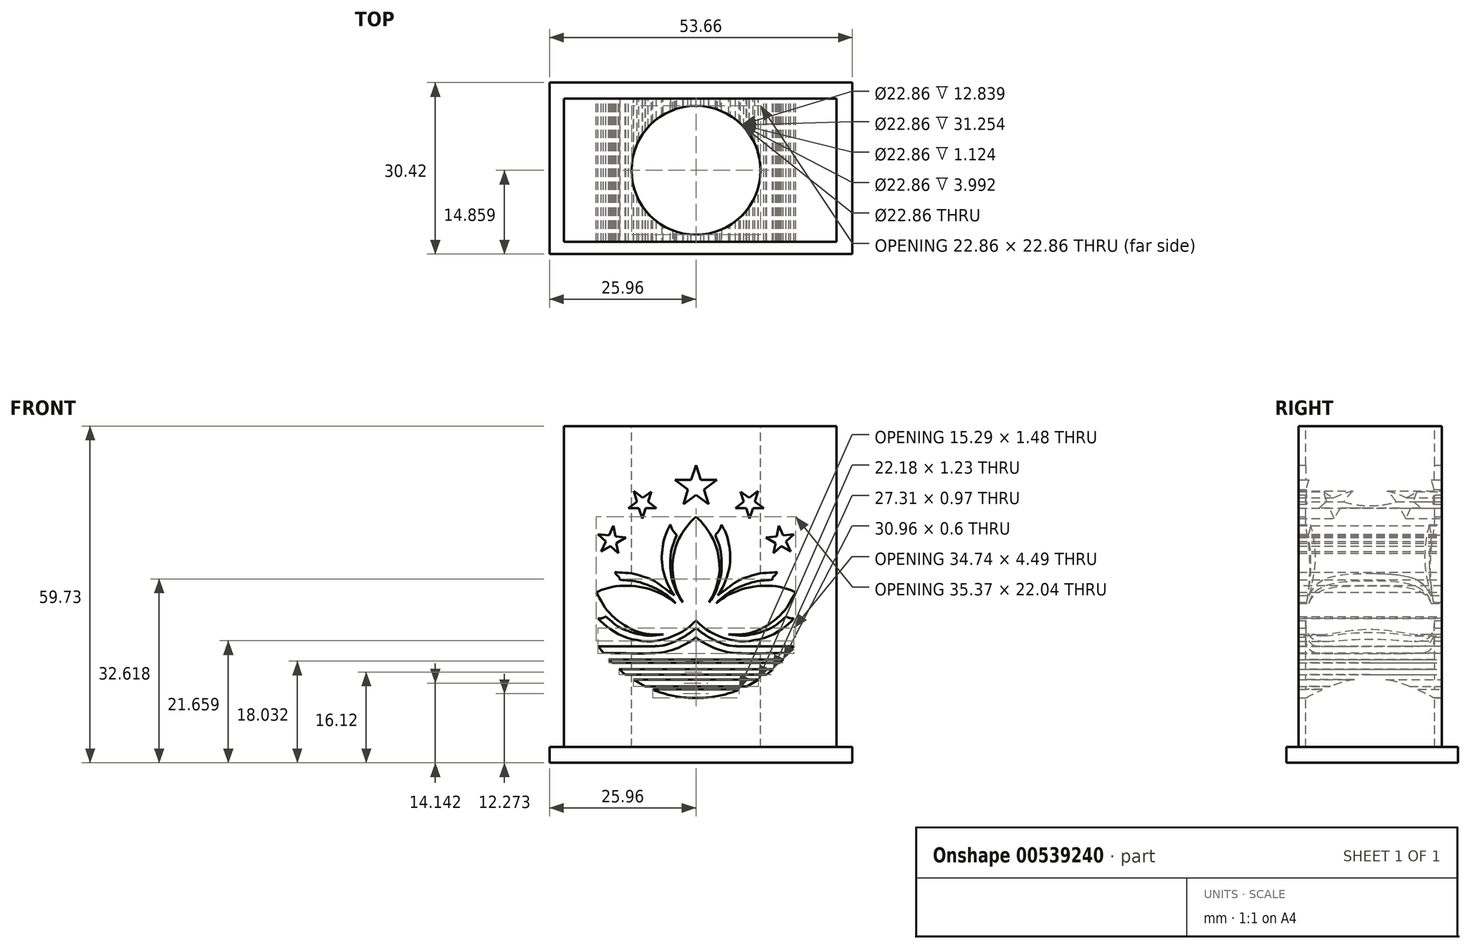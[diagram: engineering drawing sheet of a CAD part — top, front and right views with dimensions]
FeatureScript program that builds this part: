
annotation { "Feature Type Name" : "Feature", "Feature Type Description" : "" }
export const myFeature = defineFeature(function(context is Context, id is Id, definition is map)
    precondition{}
    {
        {
            var Q0;
            Q0=qCreatedBy(makeId("Front.planeOp"),FACE);
            var sketch = newSketch(context, id + "F0", { "sketchPlane" : qUnion([Q0])});
            skLineSegment(sketch, "E0.bottom", {"start": v(-23.4, 10.65) * mm, "end": v(24.88, 10.65) * mm});
            skLineSegment(sketch, "E0.top", {"start": v(-23.4, -46.28) * mm, "end": v(24.88, -46.28) * mm});
            skLineSegment(sketch, "E0.left", {"start": v(-23.4, 10.65) * mm, "end": v(-23.4, -46.28) * mm});
            skLineSegment(sketch, "E0.right", {"start": v(24.88, 10.65) * mm, "end": v(24.88, -46.28) * mm});
            skLineSegment(sketch, "E1", {"start": v(-14.67, -7.02) * mm, "end": v(-15.43, -8.75) * mm});
            skLineSegment(sketch, "E2", {"start": v(-15.43, -8.75) * mm, "end": v(-17.36, -8.56) * mm});
            skLineSegment(sketch, "E3", {"start": v(-17.36, -8.56) * mm, "end": v(-15.96, -9.83) * mm});
            skLineSegment(sketch, "E4", {"start": v(-15.96, -9.83) * mm, "end": v(-16.8, -11.56) * mm});
            skLineSegment(sketch, "E5", {"start": v(-16.8, -11.56) * mm, "end": v(-15.16, -10.63) * mm});
            skLineSegment(sketch, "E6", {"start": v(-15.16, -10.63) * mm, "end": v(-13.74, -11.88) * mm});
            skLineSegment(sketch, "E7", {"start": v(-13.74, -11.88) * mm, "end": v(-14.13, -10.12) * mm});
            skLineSegment(sketch, "E8", {"start": v(-14.13, -10.12) * mm, "end": v(-12.4, -9.14) * mm});
            skLineSegment(sketch, "E9", {"start": v(-12.4, -9.14) * mm, "end": v(-14.28, -8.92) * mm});
            skLineSegment(sketch, "E10", {"start": v(-14.67, -7.02) * mm, "end": v(-14.28, -8.92) * mm});
            skLineSegment(sketch, "E11", {"start": v(-11.02, -0.87) * mm, "end": v(-10.44, -2.79) * mm});
            skLineSegment(sketch, "E12", {"start": v(-10.44, -2.79) * mm, "end": v(-12.01, -3.9) * mm});
            skLineSegment(sketch, "E13", {"start": v(-12.01, -3.9) * mm, "end": v(-10.14, -3.9) * mm});
            skLineSegment(sketch, "E14", {"start": v(-10.14, -3.9) * mm, "end": v(-9.51, -5.75) * mm});
            skLineSegment(sketch, "E15", {"start": v(-9.51, -5.75) * mm, "end": v(-8.92, -3.9) * mm});
            skLineSegment(sketch, "E16", {"start": v(-8.92, -3.9) * mm, "end": v(-7.01, -3.9) * mm});
            skLineSegment(sketch, "E17", {"start": v(-7.01, -3.9) * mm, "end": v(-8.5, -2.75) * mm});
            skLineSegment(sketch, "E18", {"start": v(-8.5, -2.75) * mm, "end": v(-7.91, -0.98) * mm});
            skLineSegment(sketch, "E19", {"start": v(-7.91, -0.98) * mm, "end": v(-9.44, -2.07) * mm});
            skLineSegment(sketch, "E20", {"start": v(-9.44, -2.07) * mm, "end": v(-11.02, -0.87) * mm});
            skLineSegment(sketch, "E21", {"start": v(0, 3.74) * mm, "end": v(-0.86, 1.14) * mm});
            skLineSegment(sketch, "E22", {"start": v(-0.86, 1.14) * mm, "end": v(-3.73, 1.14) * mm});
            skLineSegment(sketch, "E23", {"start": v(-3.73, 1.14) * mm, "end": v(-1.44, -0.6) * mm});
            skLineSegment(sketch, "E24", {"start": v(-1.44, -0.6) * mm, "end": v(-2.21, -3.2) * mm});
            skLineSegment(sketch, "E25", {"start": v(-2.21, -3.2) * mm, "end": v(0, -1.55) * mm});
            skPoint(sketch, "E26.1.internal.snap0", {"position": v(-1.1, -2.38) * mm});
            skFitSpline(sketch, "E26", {"points": [v(0, -5.44) * mm, v(-1.1, -6.5) * mm, v(-2.36, -8.25) * mm, v(-3.29, -9.91) * mm, v(-4.02, -12.68) * mm, v(-4.12, -15.63) * mm, v(-3.2, -19) * mm, v(-2.32, -20.6) * mm], "startDerivative": vector(-9.56, -8.22) * mm, "endDerivative": vector(6.99, -11.2) * mm});
            skFitSpline(sketch, "E27", {"points": [v(-3.43, -8.7) * mm, v(-3.83, -9.72) * mm, v(-4.32, -11.27) * mm, v(-4.53, -13.34) * mm, v(-4.52, -14.72) * mm, v(-4.32, -16.29) * mm, v(-3.8, -17.9) * mm, v(-3.26, -19.24) * mm, v(-2.32, -20.6) * mm], "startDerivative": vector(-3.76, -9.37) * mm, "endDerivative": vector(8.12, -10.53) * mm});
            skFitSpline(sketch, "E28", {"points": [v(-4.54, -6.83) * mm, v(-4.2, -7.68) * mm, v(-3.83, -8.2) * mm, v(-3.43, -8.7) * mm], "startDerivative": vector(0.86, -2.43) * mm, "endDerivative": vector(1.31, -1.56) * mm});
            skFitSpline(sketch, "E29", {"points": [v(-4.54, -6.83) * mm, v(-5.12, -7.96) * mm, v(-5.79, -10.03) * mm, v(-6.04, -12.2) * mm, v(-5.93, -14.38) * mm, v(-4.91, -17.56) * mm, v(-3.85, -19.4) * mm], "startDerivative": vector(-4.51, -8.08) * mm, "endDerivative": vector(6.53, -10) * mm});
            skFitSpline(sketch, "E30", {"points": [v(-14.4, -15.26) * mm, v(-13.32, -15.35) * mm, v(-11.62, -15.47) * mm, v(-10.12, -15.8) * mm, v(-8.8, -16.23) * mm, v(-7.65, -16.69) * mm, v(-6.4, -17.5) * mm, v(-5.33, -18.28) * mm, v(-3.85, -19.4) * mm], "startDerivative": vector(9.33, -0.94) * mm, "endDerivative": vector(10.87, -8.42) * mm});
            skFitSpline(sketch, "E31", {"points": [v(-14.4, -15.26) * mm, v(-14, -15.8) * mm, v(-13.58, -16.3) * mm, v(-13.53, -16.62) * mm], "startDerivative": vector(1.03, -1.42) * mm, "endDerivative": vector(-0.04, -1.22) * mm});
            skFitSpline(sketch, "E32", {"points": [v(-13.53, -16.62) * mm, v(-12.06, -16.72) * mm, v(-10.66, -16.9) * mm, v(-9.28, -17.28) * mm, v(-8.05, -17.73) * mm, v(-6.8, -18.3) * mm, v(-4.8, -19.63) * mm, v(-3.6, -20.77) * mm], "startDerivative": vector(10.7, -0.7) * mm, "endDerivative": vector(7.32, -7.59) * mm});
            skFitSpline(sketch, "E33", {"points": [v(-17.69, -18.86) * mm, v(-17.09, -18.57) * mm, v(-15.64, -18.08) * mm, v(-13.93, -17.74) * mm, v(-12.32, -17.67) * mm, v(-10.47, -17.79) * mm, v(-8.8, -18.1) * mm, v(-7.3, -18.61) * mm, v(-5.86, -19.24) * mm, v(-4.8, -19.86) * mm, v(-3.6, -20.77) * mm], "startDerivative": vector(7.87, 4.17) * mm, "endDerivative": vector(12.2, -9.6) * mm});
            skFitSpline(sketch, "E34", {"points": [v(-17.69, -18.86) * mm, v(-16.93, -20.13) * mm, v(-16, -21.7) * mm, v(-14.74, -23.06) * mm, v(-13.08, -24.4) * mm, v(-11, -25.57) * mm, v(-9.18, -26.13) * mm, v(-7.32, -26.33) * mm, v(-5.82, -26.29) * mm], "startDerivative": vector(6.8, -10.97) * mm, "endDerivative": vector(12.92, 0.8) * mm});
            skFitSpline(sketch, "E35", {"points": [v(-15.97, -23.14) * mm, v(-14.97, -24) * mm, v(-13.74, -24.95) * mm, v(-12.06, -25.7) * mm, v(-10.79, -26.13) * mm, v(-9.06, -26.46) * mm, v(-8.05, -26.54) * mm, v(-5.82, -26.29) * mm], "startDerivative": vector(7.48, -6.47) * mm, "endDerivative": vector(14.58, 2.08) * mm});
            skFitSpline(sketch, "E36", {"points": [v(-17.37, -23.45) * mm, v(-16.72, -23.43) * mm, v(-15.97, -23.14) * mm], "startDerivative": vector(1.36, -0.09) * mm, "endDerivative": vector(1.44, 0.7) * mm});
            skFitSpline(sketch, "E37", {"points": [v(-17.37, -23.45) * mm, v(-16.33, -24.5) * mm, v(-14.84, -25.57) * mm, v(-13.02, -26.6) * mm, v(-10.83, -27.24) * mm, v(-8.36, -27.52) * mm, v(-5.65, -27.16) * mm, v(-3, -26.13) * mm, v(-1.33, -25.06) * mm, v(0, -23.85) * mm], "startDerivative": vector(10.57, -11.74) * mm, "endDerivative": vector(12.8, 12.29) * mm});
            skFitSpline(sketch, "E38", {"points": [v(-17.37, -28.38) * mm, v(-6.86, -28.37) * mm, v(-4.8, -28) * mm, v(-2.32, -26.84) * mm, v(-0.98, -25.92) * mm, v(0, -25.17) * mm], "startDerivative": vector(34.16, -0.41) * mm, "endDerivative": vector(7.58, 5.86) * mm});
            skFitSpline(sketch, "E39", {"points": [v(-17.37, -28.38) * mm, v(-16.46, -29.59) * mm], "startDerivative": vector(0.91, -1.2) * mm, "endDerivative": vector(0.91, -1.2) * mm});
            skFitSpline(sketch, "E40", {"points": [v(-16.46, -29.59) * mm, v(-6.96, -29.59) * mm, v(-5.02, -29.28) * mm, v(-3, -28.61) * mm, v(-0.47, -27.18) * mm, v(0, -26.75) * mm], "startDerivative": vector(31.08, -0.58) * mm, "endDerivative": vector(3.66, 3.9) * mm});
            skLineSegment(sketch, "E41", {"start": v(-15.48, -30.75) * mm, "end": v(0, -30.75) * mm});
            skLineSegment(sketch, "E42", {"start": v(-15.48, -30.75) * mm, "end": v(-14.9, -31.35) * mm});
            skLineSegment(sketch, "E43", {"start": v(-14.9, -31.35) * mm, "end": v(0, -31.35) * mm});
            skLineSegment(sketch, "E44", {"start": v(-13.65, -32.47) * mm, "end": v(0, -32.47) * mm});
            skLineSegment(sketch, "E45", {"start": v(-13.65, -32.47) * mm, "end": v(-12.55, -33.45) * mm});
            skLineSegment(sketch, "E46", {"start": v(-12.55, -33.45) * mm, "end": v(0, -33.45) * mm});
            skLineSegment(sketch, "E47", {"start": v(-11.09, -34.32) * mm, "end": v(0, -34.32) * mm});
            skLineSegment(sketch, "E48", {"start": v(-11.09, -34.32) * mm, "end": v(-9.03, -35.55) * mm});
            skLineSegment(sketch, "E49", {"start": v(-9.03, -35.55) * mm, "end": v(0, -35.55) * mm});
            skLineSegment(sketch, "E50", {"start": v(0, -35.55) * mm, "end": v(-0.04, -35.49) * mm});
            skLineSegment(sketch, "E51", {"start": v(0, -36.07) * mm, "end": v(-7.65, -36.07) * mm});
            skFitSpline(sketch, "E52", {"points": [v(-7.65, -36.07) * mm, v(-7.38, -36.24) * mm, v(-7.03, -36.38) * mm, v(-6.63, -36.5) * mm, v(-6.21, -36.63) * mm, v(-5.67, -36.78) * mm, v(-4.93, -37) * mm, v(-4.25, -37.15) * mm, v(-3.34, -37.34) * mm, v(-2.37, -37.47) * mm, v(-1.32, -37.55) * mm, v(0, -37.55) * mm], "startDerivative": vector(3.96, -3.13) * mm, "endDerivative": vector(10.75, 0.18) * mm});
            skLineSegment(sketch, "E53", {"start": v(0, 3.74) * mm, "end": v(0, -37.55) * mm});
            skLineSegment(sketch, "E54.MirrorCS", {"start": v(0, 3.74) * mm, "end": v(0.86, 1.14) * mm});
            skLineSegment(sketch, "E55.MirrorCS", {"start": v(0.86, 1.14) * mm, "end": v(3.73, 1.14) * mm});
            skLineSegment(sketch, "E56.MirrorCS", {"start": v(3.73, 1.14) * mm, "end": v(1.44, -0.6) * mm});
            skLineSegment(sketch, "E57.MirrorCS", {"start": v(1.44, -0.6) * mm, "end": v(2.21, -3.2) * mm});
            skPoint(sketch, "E58.MirrorP", {"position": v(1.1, -2.38) * mm});
            skLineSegment(sketch, "E59.MirrorCS", {"start": v(2.21, -3.2) * mm, "end": v(0, -1.55) * mm});
            skLineSegment(sketch, "E60.MirrorCS", {"start": v(9.44, -2.07) * mm, "end": v(11.02, -0.87) * mm});
            skLineSegment(sketch, "E61.MirrorCS", {"start": v(11.02, -0.87) * mm, "end": v(10.44, -2.79) * mm});
            skLineSegment(sketch, "E62.MirrorCS", {"start": v(10.44, -2.79) * mm, "end": v(12.01, -3.9) * mm});
            skLineSegment(sketch, "E63.MirrorCS", {"start": v(12.01, -3.9) * mm, "end": v(10.14, -3.9) * mm});
            skLineSegment(sketch, "E64.MirrorCS", {"start": v(10.14, -3.9) * mm, "end": v(9.51, -5.75) * mm});
            skLineSegment(sketch, "E65.MirrorCS", {"start": v(9.51, -5.75) * mm, "end": v(8.92, -3.9) * mm});
            skLineSegment(sketch, "E66.MirrorCS", {"start": v(8.92, -3.9) * mm, "end": v(7.01, -3.9) * mm});
            skLineSegment(sketch, "E67.MirrorCS", {"start": v(7.01, -3.9) * mm, "end": v(8.5, -2.75) * mm});
            skLineSegment(sketch, "E68.MirrorCS", {"start": v(8.5, -2.75) * mm, "end": v(7.91, -0.98) * mm});
            skLineSegment(sketch, "E69.MirrorCS", {"start": v(7.91, -0.98) * mm, "end": v(9.44, -2.07) * mm});
            skLineSegment(sketch, "E70.MirrorCS", {"start": v(14.67, -7.02) * mm, "end": v(15.43, -8.75) * mm});
            skLineSegment(sketch, "E71.MirrorCS", {"start": v(15.43, -8.75) * mm, "end": v(17.36, -8.56) * mm});
            skLineSegment(sketch, "E72.MirrorCS", {"start": v(17.36, -8.56) * mm, "end": v(15.96, -9.83) * mm});
            skLineSegment(sketch, "E73.MirrorCS", {"start": v(15.96, -9.83) * mm, "end": v(16.8, -11.56) * mm});
            skLineSegment(sketch, "E74.MirrorCS", {"start": v(16.8, -11.56) * mm, "end": v(15.16, -10.63) * mm});
            skLineSegment(sketch, "E75.MirrorCS", {"start": v(15.16, -10.63) * mm, "end": v(13.74, -11.88) * mm});
            skLineSegment(sketch, "E76.MirrorCS", {"start": v(13.74, -11.88) * mm, "end": v(14.13, -10.12) * mm});
            skLineSegment(sketch, "E77.MirrorCS", {"start": v(14.13, -10.12) * mm, "end": v(12.4, -9.14) * mm});
            skLineSegment(sketch, "E78.MirrorCS", {"start": v(12.4, -9.14) * mm, "end": v(14.28, -8.92) * mm});
            skLineSegment(sketch, "E79.MirrorCS", {"start": v(14.67, -7.02) * mm, "end": v(14.28, -8.92) * mm});
            skFitSpline(sketch, "E80.MirrorCS", {"points": [v(0, -5.44) * mm, v(1.1, -6.5) * mm, v(2.36, -8.25) * mm, v(3.29, -9.91) * mm, v(4.02, -12.68) * mm, v(4.12, -15.63) * mm, v(3.2, -19) * mm, v(2.32, -20.6) * mm], "startDerivative": vector(9.56, -8.22) * mm, "endDerivative": vector(-6.99, -11.2) * mm});
            skFitSpline(sketch, "E81.MirrorCS", {"points": [v(3.43, -8.7) * mm, v(3.83, -9.72) * mm, v(4.32, -11.27) * mm, v(4.53, -13.34) * mm, v(4.52, -14.72) * mm, v(4.32, -16.29) * mm, v(3.8, -17.9) * mm, v(3.26, -19.24) * mm, v(2.32, -20.6) * mm], "startDerivative": vector(3.76, -9.37) * mm, "endDerivative": vector(-8.12, -10.53) * mm});
            skFitSpline(sketch, "E82.MirrorCS", {"points": [v(4.54, -6.83) * mm, v(4.2, -7.68) * mm, v(3.83, -8.2) * mm, v(3.43, -8.7) * mm], "startDerivative": vector(-0.86, -2.43) * mm, "endDerivative": vector(-1.31, -1.56) * mm});
            skFitSpline(sketch, "E83.MirrorCS", {"points": [v(4.54, -6.83) * mm, v(5.12, -7.96) * mm, v(5.79, -10.03) * mm, v(6.04, -12.2) * mm, v(5.93, -14.38) * mm, v(4.91, -17.56) * mm, v(3.85, -19.4) * mm], "startDerivative": vector(4.51, -8.08) * mm, "endDerivative": vector(-6.53, -10) * mm});
            skFitSpline(sketch, "E84.MirrorCS", {"points": [v(14.4, -15.26) * mm, v(13.32, -15.35) * mm, v(11.62, -15.47) * mm, v(10.12, -15.8) * mm, v(8.8, -16.23) * mm, v(7.65, -16.69) * mm, v(6.4, -17.5) * mm, v(5.33, -18.28) * mm, v(3.85, -19.4) * mm], "startDerivative": vector(-9.33, -0.94) * mm, "endDerivative": vector(-10.87, -8.42) * mm});
            skFitSpline(sketch, "E85.MirrorCS", {"points": [v(14.4, -15.26) * mm, v(14, -15.8) * mm, v(13.58, -16.3) * mm, v(13.53, -16.62) * mm], "startDerivative": vector(-1.03, -1.42) * mm, "endDerivative": vector(0.04, -1.22) * mm});
            skFitSpline(sketch, "E86.MirrorCS", {"points": [v(13.53, -16.62) * mm, v(12.06, -16.72) * mm, v(10.66, -16.9) * mm, v(9.28, -17.28) * mm, v(8.05, -17.73) * mm, v(6.8, -18.3) * mm, v(4.8, -19.63) * mm, v(3.6, -20.77) * mm], "startDerivative": vector(-10.7, -0.7) * mm, "endDerivative": vector(-7.32, -7.59) * mm});
            skFitSpline(sketch, "E87.MirrorCS", {"points": [v(17.69, -18.86) * mm, v(17.09, -18.57) * mm, v(15.64, -18.08) * mm, v(13.93, -17.74) * mm, v(12.32, -17.67) * mm, v(10.47, -17.79) * mm, v(8.8, -18.1) * mm, v(7.3, -18.61) * mm, v(5.86, -19.24) * mm, v(4.8, -19.86) * mm, v(3.6, -20.77) * mm], "startDerivative": vector(-7.87, 4.17) * mm, "endDerivative": vector(-12.2, -9.6) * mm});
            skFitSpline(sketch, "E88.MirrorCS", {"points": [v(17.69, -18.86) * mm, v(16.93, -20.13) * mm, v(16, -21.7) * mm, v(14.74, -23.06) * mm, v(13.08, -24.4) * mm, v(11, -25.57) * mm, v(9.18, -26.13) * mm, v(7.32, -26.33) * mm, v(5.82, -26.29) * mm], "startDerivative": vector(-6.8, -10.97) * mm, "endDerivative": vector(-12.92, 0.8) * mm});
            skFitSpline(sketch, "E89.MirrorCS", {"points": [v(17.37, -28.38) * mm, v(6.86, -28.37) * mm, v(4.8, -28) * mm, v(2.32, -26.84) * mm, v(0.98, -25.92) * mm, v(0, -25.17) * mm], "startDerivative": vector(-34.16, -0.41) * mm, "endDerivative": vector(-7.58, 5.86) * mm});
            skFitSpline(sketch, "E90.MirrorCS", {"points": [v(16.46, -29.59) * mm, v(6.96, -29.59) * mm, v(5.02, -29.28) * mm, v(3, -28.61) * mm, v(0.47, -27.18) * mm, v(0, -26.75) * mm], "startDerivative": vector(-31.08, -0.58) * mm, "endDerivative": vector(-3.66, 3.9) * mm});
            skLineSegment(sketch, "E91.MirrorCS", {"start": v(15.48, -30.75) * mm, "end": v(0, -30.75) * mm});
            skFitSpline(sketch, "E92.MirrorCS", {"points": [v(17.37, -28.38) * mm, v(16.46, -29.59) * mm], "startDerivative": vector(-0.91, -1.2) * mm, "endDerivative": vector(-0.91, -1.2) * mm});
            skLineSegment(sketch, "E93.MirrorCS", {"start": v(15.48, -30.75) * mm, "end": v(14.9, -31.35) * mm});
            skLineSegment(sketch, "E94.MirrorCS", {"start": v(14.9, -31.35) * mm, "end": v(0, -31.35) * mm});
            skLineSegment(sketch, "E95.MirrorCS", {"start": v(13.65, -32.47) * mm, "end": v(0, -32.47) * mm});
            skLineSegment(sketch, "E96.MirrorCS", {"start": v(13.65, -32.47) * mm, "end": v(12.55, -33.45) * mm});
            skLineSegment(sketch, "E97.MirrorCS", {"start": v(12.55, -33.45) * mm, "end": v(0, -33.45) * mm});
            skLineSegment(sketch, "E98.MirrorCS", {"start": v(11.09, -34.32) * mm, "end": v(0, -34.32) * mm});
            skLineSegment(sketch, "E99.MirrorCS", {"start": v(11.09, -34.32) * mm, "end": v(9.03, -35.55) * mm});
            skLineSegment(sketch, "E100.MirrorCS", {"start": v(9.03, -35.55) * mm, "end": v(0, -35.55) * mm});
            skLineSegment(sketch, "E101.MirrorCS", {"start": v(0, -36.07) * mm, "end": v(7.65, -36.07) * mm});
            skFitSpline(sketch, "E102.MirrorCS", {"points": [v(7.65, -36.07) * mm, v(7.38, -36.24) * mm, v(7.03, -36.38) * mm, v(6.63, -36.5) * mm, v(6.21, -36.63) * mm, v(5.67, -36.78) * mm, v(4.93, -37) * mm, v(4.25, -37.15) * mm, v(3.34, -37.34) * mm, v(2.37, -37.47) * mm, v(1.32, -37.55) * mm, v(0, -37.55) * mm], "startDerivative": vector(-3.96, -3.13) * mm, "endDerivative": vector(-10.75, 0.18) * mm});
            skFitSpline(sketch, "E103.MirrorCS", {"points": [v(17.37, -23.45) * mm, v(16.33, -24.5) * mm, v(14.84, -25.57) * mm, v(13.02, -26.6) * mm, v(10.83, -27.24) * mm, v(8.36, -27.52) * mm, v(5.65, -27.16) * mm, v(3, -26.13) * mm, v(1.33, -25.06) * mm, v(0, -23.85) * mm], "startDerivative": vector(-10.57, -11.74) * mm, "endDerivative": vector(-12.8, 12.29) * mm});
            skFitSpline(sketch, "E104.MirrorCS", {"points": [v(15.97, -23.14) * mm, v(14.97, -24) * mm, v(13.74, -24.95) * mm, v(12.06, -25.7) * mm, v(10.79, -26.13) * mm, v(9.06, -26.46) * mm, v(8.05, -26.54) * mm, v(5.82, -26.29) * mm], "startDerivative": vector(-7.48, -6.47) * mm, "endDerivative": vector(-14.58, 2.08) * mm});
            skFitSpline(sketch, "E105.MirrorCS", {"points": [v(17.37, -23.45) * mm, v(16.72, -23.43) * mm, v(15.97, -23.14) * mm], "startDerivative": vector(-1.36, -0.09) * mm, "endDerivative": vector(-1.44, 0.7) * mm});
            skSolve(sketch);
        }
        {
            var Q0;
            Q0 = qSketchRegion(id + "F0", true);
            extrude(context, id + "F1", {"entities" : qUnion([Q0]), "depth" : 25.4 * mm, "offsetDistance" : 25.4 * mm});
        }
        {
            var Q0;
            Q0=makeQuery(id+"F1.opExtrude","SWEPT_FACE",FACE,{"disambiguationData":[OSD([sQuery(id+"F0.wireOp",EDGE,"E0.bottom")])]});
            var sketch = newSketch(context, id + "F2", { "sketchPlane" : qUnion([Q0])});
            skCircle(sketch, "E106", {"center": v(0, -12.72) * mm, "radius": 10.99 * mm});
            skSolve(sketch);
        }
        {
            var Q0;
            Q0=sQuery(id+"F2.wireOp",VERTEX,"E106.center");
            var Q1;
            Q1=makeQuery(id+"F1.opExtrude","SWEPT_BODY",BODY,{"disambiguationData":[OSD([sQuery(id+"F0.wireOp",EDGE,"E0.bottom"),sQuery(id+"F0.wireOp",EDGE,"E0.top"),sQuery(id+"F0.wireOp",EDGE,"E0.left"),sQuery(id+"F0.wireOp",EDGE,"E0.right"),sQuery(id+"F0.wireOp",EDGE,"E1"),sQuery(id+"F0.wireOp",EDGE,"E2"),sQuery(id+"F0.wireOp",EDGE,"E3"),sQuery(id+"F0.wireOp",EDGE,"E4"),sQuery(id+"F0.wireOp",EDGE,"E5"),sQuery(id+"F0.wireOp",EDGE,"E6"),sQuery(id+"F0.wireOp",EDGE,"E7"),sQuery(id+"F0.wireOp",EDGE,"E8"),sQuery(id+"F0.wireOp",EDGE,"E9"),sQuery(id+"F0.wireOp",EDGE,"E10"),sQuery(id+"F0.wireOp",EDGE,"E11"),sQuery(id+"F0.wireOp",EDGE,"E12"),sQuery(id+"F0.wireOp",EDGE,"E13"),sQuery(id+"F0.wireOp",EDGE,"E14"),sQuery(id+"F0.wireOp",EDGE,"E15"),sQuery(id+"F0.wireOp",EDGE,"E16"),sQuery(id+"F0.wireOp",EDGE,"E17"),sQuery(id+"F0.wireOp",EDGE,"E18"),sQuery(id+"F0.wireOp",EDGE,"E19"),sQuery(id+"F0.wireOp",EDGE,"E20"),sQuery(id+"F0.wireOp",EDGE,"E21"),sQuery(id+"F0.wireOp",EDGE,"E22"),sQuery(id+"F0.wireOp",EDGE,"E23"),sQuery(id+"F0.wireOp",EDGE,"E24"),sQuery(id+"F0.wireOp",EDGE,"E25"),sQuery(id+"F0.wireOp",EDGE,"E26"),sQuery(id+"F0.wireOp",EDGE,"E27"),sQuery(id+"F0.wireOp",EDGE,"E28"),sQuery(id+"F0.wireOp",EDGE,"E29"),sQuery(id+"F0.wireOp",EDGE,"E30"),sQuery(id+"F0.wireOp",EDGE,"E31"),sQuery(id+"F0.wireOp",EDGE,"E32"),sQuery(id+"F0.wireOp",EDGE,"E33"),sQuery(id+"F0.wireOp",EDGE,"E34"),sQuery(id+"F0.wireOp",EDGE,"E35"),sQuery(id+"F0.wireOp",EDGE,"E36"),sQuery(id+"F0.wireOp",EDGE,"E37"),sQuery(id+"F0.wireOp",EDGE,"E38"),sQuery(id+"F0.wireOp",EDGE,"E39"),sQuery(id+"F0.wireOp",EDGE,"E40"),sQuery(id+"F0.wireOp",EDGE,"E41"),sQuery(id+"F0.wireOp",EDGE,"E42"),sQuery(id+"F0.wireOp",EDGE,"E43"),sQuery(id+"F0.wireOp",EDGE,"E44"),sQuery(id+"F0.wireOp",EDGE,"E45"),sQuery(id+"F0.wireOp",EDGE,"E46"),sQuery(id+"F0.wireOp",EDGE,"E47"),sQuery(id+"F0.wireOp",EDGE,"E48"),sQuery(id+"F0.wireOp",EDGE,"E49"),sQuery(id+"F0.wireOp",EDGE,"E51"),sQuery(id+"F0.wireOp",EDGE,"E52"),sQuery(id+"F0.wireOp",EDGE,"E54.MirrorCS"),sQuery(id+"F0.wireOp",EDGE,"E55.MirrorCS"),sQuery(id+"F0.wireOp",EDGE,"E56.MirrorCS"),sQuery(id+"F0.wireOp",EDGE,"E57.MirrorCS"),sQuery(id+"F0.wireOp",EDGE,"E59.MirrorCS"),sQuery(id+"F0.wireOp",EDGE,"E60.MirrorCS"),sQuery(id+"F0.wireOp",EDGE,"E61.MirrorCS"),sQuery(id+"F0.wireOp",EDGE,"E62.MirrorCS"),sQuery(id+"F0.wireOp",EDGE,"E63.MirrorCS"),sQuery(id+"F0.wireOp",EDGE,"E64.MirrorCS"),sQuery(id+"F0.wireOp",EDGE,"E65.MirrorCS"),sQuery(id+"F0.wireOp",EDGE,"E66.MirrorCS"),sQuery(id+"F0.wireOp",EDGE,"E67.MirrorCS"),sQuery(id+"F0.wireOp",EDGE,"E68.MirrorCS"),sQuery(id+"F0.wireOp",EDGE,"E69.MirrorCS"),sQuery(id+"F0.wireOp",EDGE,"E70.MirrorCS"),sQuery(id+"F0.wireOp",EDGE,"E71.MirrorCS"),sQuery(id+"F0.wireOp",EDGE,"E72.MirrorCS"),sQuery(id+"F0.wireOp",EDGE,"E73.MirrorCS"),sQuery(id+"F0.wireOp",EDGE,"E74.MirrorCS"),sQuery(id+"F0.wireOp",EDGE,"E75.MirrorCS"),sQuery(id+"F0.wireOp",EDGE,"E76.MirrorCS"),sQuery(id+"F0.wireOp",EDGE,"E77.MirrorCS"),sQuery(id+"F0.wireOp",EDGE,"E78.MirrorCS"),sQuery(id+"F0.wireOp",EDGE,"E79.MirrorCS"),sQuery(id+"F0.wireOp",EDGE,"E80.MirrorCS"),sQuery(id+"F0.wireOp",EDGE,"E81.MirrorCS"),sQuery(id+"F0.wireOp",EDGE,"E82.MirrorCS"),sQuery(id+"F0.wireOp",EDGE,"E83.MirrorCS"),sQuery(id+"F0.wireOp",EDGE,"E84.MirrorCS"),sQuery(id+"F0.wireOp",EDGE,"E85.MirrorCS"),sQuery(id+"F0.wireOp",EDGE,"E86.MirrorCS"),sQuery(id+"F0.wireOp",EDGE,"E87.MirrorCS"),sQuery(id+"F0.wireOp",EDGE,"E88.MirrorCS"),sQuery(id+"F0.wireOp",EDGE,"E89.MirrorCS"),sQuery(id+"F0.wireOp",EDGE,"E90.MirrorCS"),sQuery(id+"F0.wireOp",EDGE,"E91.MirrorCS"),sQuery(id+"F0.wireOp",EDGE,"E92.MirrorCS"),sQuery(id+"F0.wireOp",EDGE,"E93.MirrorCS"),sQuery(id+"F0.wireOp",EDGE,"E94.MirrorCS"),sQuery(id+"F0.wireOp",EDGE,"E95.MirrorCS"),sQuery(id+"F0.wireOp",EDGE,"E96.MirrorCS"),sQuery(id+"F0.wireOp",EDGE,"E97.MirrorCS"),sQuery(id+"F0.wireOp",EDGE,"E98.MirrorCS"),sQuery(id+"F0.wireOp",EDGE,"E99.MirrorCS"),sQuery(id+"F0.wireOp",EDGE,"E100.MirrorCS"),sQuery(id+"F0.wireOp",EDGE,"E101.MirrorCS"),sQuery(id+"F0.wireOp",EDGE,"E102.MirrorCS"),sQuery(id+"F0.wireOp",EDGE,"E103.MirrorCS"),sQuery(id+"F0.wireOp",EDGE,"E104.MirrorCS"),sQuery(id+"F0.wireOp",EDGE,"E105.MirrorCS")])]});
            hole(context, id + "F3", {"style" : HoleStyle.SIMPLE, "endStyle" : HoleEndStyle.THROUGH, "holeDiameter" : 22.86 * mm, "isTappedThrough" : true, "tappedDepth" : 12.7 * mm, "tapClearance" : 3, "locations" : qUnion([Q0]), "scope" : qUnion([Q1])});
        }
        {
            var Q0;
            Q0=makeQuery(id+"F1.opExtrude","SWEPT_FACE",FACE,{"disambiguationData":[OSD([sQuery(id+"F0.wireOp",EDGE,"E0.top")])]});
            var sketch = newSketch(context, id + "F4", { "sketchPlane" : qUnion([Q0])});
            skLineSegment(sketch, "E107.bottom", {"start": v(-23.4, 25.4) * mm, "end": v(24.88, 25.4) * mm});
            skLineSegment(sketch, "E107.top", {"start": v(-23.4, 0) * mm, "end": v(24.88, 0) * mm});
            skLineSegment(sketch, "E107.left", {"start": v(-23.4, 25.4) * mm, "end": v(-23.4, 0) * mm});
            skLineSegment(sketch, "E107.right", {"start": v(24.88, 25.4) * mm, "end": v(24.88, 0) * mm});
            skSolve(sketch);
        }
        {
            var Q0;
            Q0=makeQuery(id+"F4.imprint","IMPRINT",FACE,{"disambiguationData":[TD([[makeQuery(id+"F4.imprint","IMPRINT",EDGE,{"derivedFrom":sQuery(id+"F4.wireOp",EDGE,"E107.bottom")}),-1.0]])]});
            var sketch = newSketch(context, id + "F5", { "sketchPlane" : qUnion([Q0])});
            skLineSegment(sketch, "E108.bottom", {"start": v(-25.96, 27.58) * mm, "end": v(27.7, 27.58) * mm});
            skLineSegment(sketch, "E108.top", {"start": v(-25.96, -2.84) * mm, "end": v(27.7, -2.84) * mm});
            skLineSegment(sketch, "E108.left", {"start": v(-25.96, 27.58) * mm, "end": v(-25.96, -2.84) * mm});
            skLineSegment(sketch, "E108.right", {"start": v(27.7, 27.58) * mm, "end": v(27.7, -2.84) * mm});
            skSolve(sketch);
        }
        {
            var Q0;
            Q0 = qSketchRegion(id + "F5", true);
            extrude(context, id + "F6", {"entities" : qUnion([Q0]), "operationType" : NewBodyOperationType.ADD, "depth" : 2.8 * mm, "offsetDistance" : 25.4 * mm});
        }
    });
